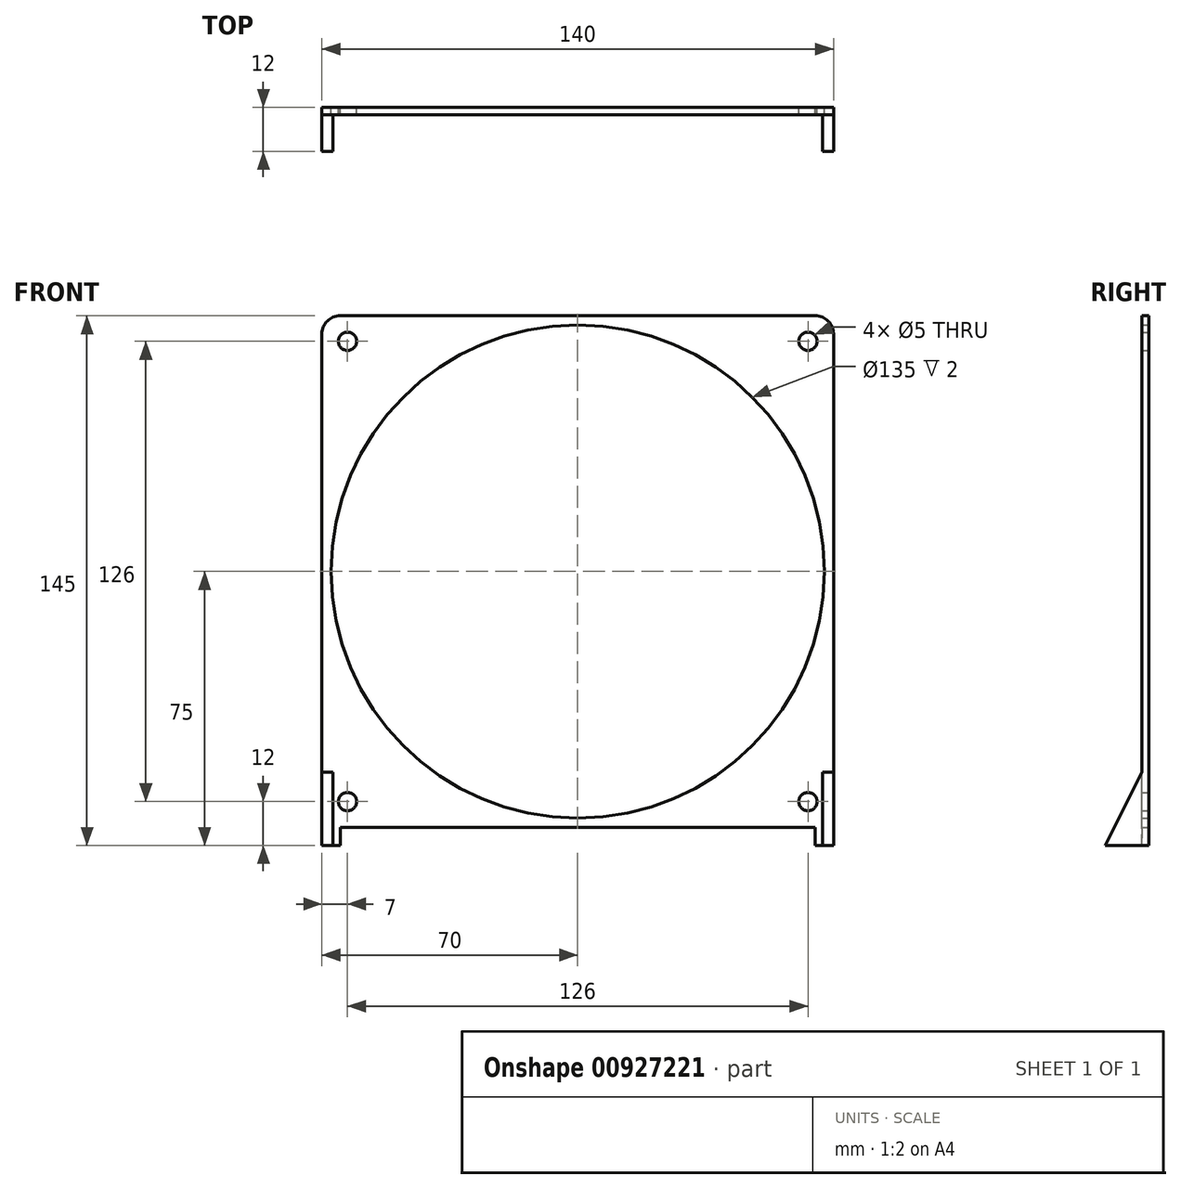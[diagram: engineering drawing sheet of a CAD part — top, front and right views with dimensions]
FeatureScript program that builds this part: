
annotation { "Feature Type Name" : "Feature", "Feature Type Description" : "" }
export const myFeature = defineFeature(function(context is Context, id is Id, definition is map)
    precondition{}
    {
        {
            var Q0;
            Q0=qCreatedBy(makeId("Front.planeOp"),FACE);
            var sketch = newSketch(context, id + "F0", { "sketchPlane" : qUnion([Q0])});
            skLineSegment(sketch, "E0.bottom", {"start": v(-65, -70) * mm, "end": v(65, -70) * mm});
            skLineSegment(sketch, "E0.top", {"start": v(-65, 70) * mm, "end": v(65, 70) * mm});
            skLineSegment(sketch, "E0.left", {"start": v(-70, -75) * mm, "end": v(-70, 65) * mm});
            skLineSegment(sketch, "E0.right", {"start": v(70, -75) * mm, "end": v(70, 65) * mm});
            skCircle(sketch, "E1", {"center": v(-63, 63) * mm, "radius": 2.5 * mm});
            skLineSegment(sketch, "E2", {"start": v(0, -74.7) * mm, "end": v(0, 75.73) * mm, "construction": true});
            skPoint(sketch, "E2.endSnap0", {"position": v(0, 70) * mm});
            skLineSegment(sketch, "E3", {"start": v(-74.67, 0) * mm, "end": v(75.27, 0) * mm, "construction": true});
            skCircle(sketch, "E4.MirrorC", {"center": v(63, 63) * mm, "radius": 2.5 * mm});
            skLineSegment(sketch, "E5.MirrorCS", {"start": v(74.67, 0) * mm, "end": v(-75.27, 0) * mm, "construction": true});
            skCircle(sketch, "E6.MirrorC", {"center": v(63, -63) * mm, "radius": 2.5 * mm});
            skCircle(sketch, "E7.MirrorC", {"center": v(-63, -63) * mm, "radius": 2.5 * mm});
            skPoint(sketch, "E8.visualSharp", {"position": v(-70, 70) * mm});
            skArc(sketch, "E8.filletArc", {"start": v(-65, 70) * mm, "mid": v(-68.54, 68.54) * mm, "end": v(-70, 65) * mm});
            skPoint(sketch, "E9.visualSharp", {"position": v(70, 70) * mm});
            skArc(sketch, "E9.filletArc", {"start": v(70, 65) * mm, "mid": v(68.54, 68.54) * mm, "end": v(65, 70) * mm});
            skPoint(sketch, "E10.visualSharp", {"position": v(-70, -70) * mm});
            skPoint(sketch, "E11.visualSharp", {"position": v(70, -70) * mm});
            skCircle(sketch, "E12", {"center": v(0, 0) * mm, "radius": 67.5 * mm});
            skLineSegment(sketch, "E13", {"start": v(-65, -70) * mm, "end": v(-65, -75) * mm});
            skLineSegment(sketch, "E14", {"start": v(-65, -75) * mm, "end": v(-70, -75) * mm});
            skLineSegment(sketch, "E15", {"start": v(65, -70) * mm, "end": v(65, -75) * mm});
            skPoint(sketch, "E15.endSnap0", {"position": v(-67.5, -75) * mm});
            skLineSegment(sketch, "E16", {"start": v(65, -75) * mm, "end": v(70, -75) * mm});
            skSolve(sketch);
        }
        {
            var Q0;
            Q0 = qSketchRegion(id + "F0", true);
            extrude(context, id + "F1", {"entities" : qUnion([Q0]), "depth" : 2 * mm, "offsetDistance" : 25 * mm});
        }
        {
            var Q0;
            Q0=makeQuery(id+"F1.opExtrude","SWEPT_FACE",FACE,{"disambiguationData":[OSD([sQuery(id+"F0.wireOp",EDGE,"E0.left")])]});
            var sketch = newSketch(context, id + "F2", { "sketchPlane" : qUnion([Q0])});
            skLineSegment(sketch, "E17", {"start": v(2, -75) * mm, "end": v(12, -75) * mm});
            skLineSegment(sketch, "E18", {"start": v(12, -75) * mm, "end": v(2, -55) * mm});
            skLineSegment(sketch, "E19", {"start": v(2, -55) * mm, "end": v(2, -75) * mm});
            skSolve(sketch);
        }
        {
            var Q0;
            Q0 = qSketchRegion(id + "F2", true);
            extrude(context, id + "F3", {"entities" : qUnion([Q0]), "oppositeDirection" : true, "depth" : 3 * mm, "offsetDistance" : 25 * mm});
        }
        {
            var Q0;
            Q0=makeQuery(id+"F1.opExtrude","SWEPT_FACE",FACE,{"disambiguationData":[OSD([sQuery(id+"F0.wireOp",EDGE,"E0.right")])]});
            var sketch = newSketch(context, id + "F4", { "sketchPlane" : qUnion([Q0])});
            skLineSegment(sketch, "E20", {"start": v(-2, -75) * mm, "end": v(-12, -75) * mm});
            skLineSegment(sketch, "E21", {"start": v(-12, -75) * mm, "end": v(-2, -55) * mm});
            skLineSegment(sketch, "E22", {"start": v(-2, -55) * mm, "end": v(-2, -75) * mm});
            skSolve(sketch);
        }
        {
            var Q0;
            Q0 = qSketchRegion(id + "F4", true);
            extrude(context, id + "F5", {"entities" : qUnion([Q0]), "operationType" : NewBodyOperationType.ADD, "oppositeDirection" : true, "depth" : 3 * mm, "offsetDistance" : 25 * mm});
        }
    });
